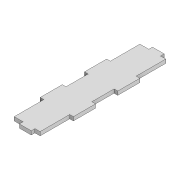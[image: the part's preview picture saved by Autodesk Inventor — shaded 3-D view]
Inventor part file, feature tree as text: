
AUTODESK INVENTOR PART (.ipt)
format: ipt  version: 2022 (Build 260153000, 153)  size: 113,152 bytes
history: native  units: mm
features: extrude x1, sketch x1
ambient origin geometry x8: Origin, YZ Plane, XZ Plane, XY Plane, X Axis, Y Axis, Z Axis, Center Point
bodies: Body1 (feature_tree)
feature tree (2):
  extrude  "Extrusion2"  Depth=170.0mm
  sketch  "Sketch1"  dims[d22=35.0mm d23=170.0mm d24=16.0mm d25=5.0mm d26=12.0mm d27=5.0mm d28=30.0mm d29=5.0mm d30=30.0mm d31=30.0mm d32=40.0mm d33=5.0mm d34=16.0mm d35=5.0mm d36=5.0mm d37=0.0mm]
